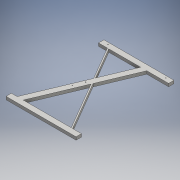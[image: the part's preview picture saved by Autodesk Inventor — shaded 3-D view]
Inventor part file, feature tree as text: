
AUTODESK INVENTOR PART (.ipt)
format: ipt  version: 2016 (Build 200138000, 138)  size: 146,432 bytes
history: native  units: mm
features: extrude x2, thread x2, sketch x2
ambient origin geometry x8: Origin, YZ Plane, XZ Plane, XY Plane, X Axis, Y Axis, Z Axis, Center Point
bodies: 实体1 (feature_tree)
feature tree (6):
  extrude  "拉伸1"  Depth=40.0mm
  extrude  "拉伸2"  Depth=10.0mm
  thread  "螺纹1"  [1 undecoded]
  thread  "螺纹2"  [1 undecoded]
  sketch  "草图1"  dims[d0=520.0mm d1=40.0mm]
  sketch  "草图2"  dims[d2=162.0mm d3=45.0mm d4=647.0mm d5=40.0mm d6=43.0mm d7=66.0mm d8=66.0mm d9=10.0mm d10=22.0mm d11=0.0mm d12=45.0mm d13=5.0mm d14=15.0mm d15=45.0mm d16=15.0mm d17=5.0mm d23=25.0mm d24=0.0mm d46=5.0mm d47=5.0mm d48=75.0mm d49=10.0mm d50=0.0mm d51=10.0mm d52=0.0mm]
note: 2 required parameter values undecoded (feature->parameter linkage not recoverable at this tier; creation-order binding heuristic only, values carry confidence <= 0.55)
